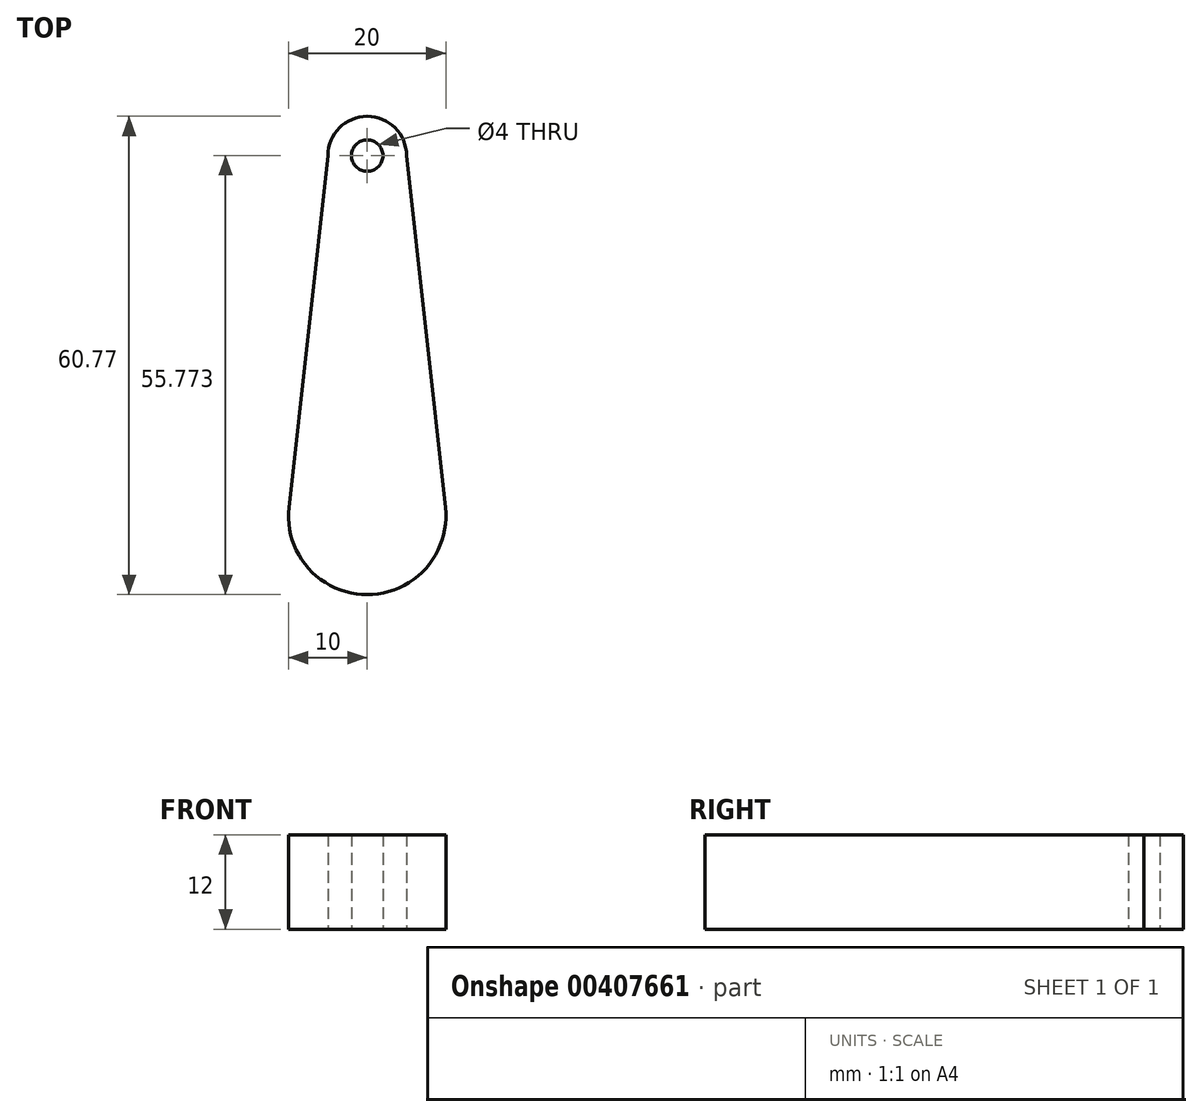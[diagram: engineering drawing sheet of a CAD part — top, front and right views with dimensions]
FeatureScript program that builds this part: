
annotation { "Feature Type Name" : "Feature", "Feature Type Description" : "" }
export const myFeature = defineFeature(function(context is Context, id is Id, definition is map)
    precondition{}
    {
        {
            var Q0;
            Q0=qCreatedBy(makeId("Top.planeOp"),FACE);
            var sketch = newSketch(context, id + "F0", { "sketchPlane" : qUnion([Q0])});
            skCircle(sketch, "E0", {"center": v(0, 0) * mm, "radius": 10 * mm});
            skCircle(sketch, "E1", {"center": v(0, 45.77) * mm, "radius": 5 * mm});
            skLineSegment(sketch, "E2", {"start": v(5, 45.77) * mm, "end": v(10.06, 0) * mm});
            skLineSegment(sketch, "E3", {"start": v(-5, 45.77) * mm, "end": v(-10.06, 0) * mm});
            skCircle(sketch, "E4", {"center": v(0, 45.77) * mm, "radius": 2 * mm});
            skSolve(sketch);
        }
        {
            var Q0;
            {var subQ0=sQuery(id+"F0.wireOp",EDGE,"E0");var subQ1=makeQuery(id+"F0.imprint","INTERSECT",VERTEX,{"derivedFrom":[subQ0,sQuery(id+"F0.wireOp",EDGE,"E2")]});Q0=makeQuery(id+"F0.imprint","IMPRINT",FACE,{"disambiguationData":[TD([[makeQuery(id+"F0.imprint","IMPRINT",EDGE,{"disambiguationData":[TD([[subQ1,-1.0]])],"derivedFrom":subQ0}),1.0]])]});}
            var Q1;
            {var subQ0=sQuery(id+"F0.wireOp",EDGE,"E1");var subQ1=makeQuery(id+"F0.imprint","INTERSECT",VERTEX,{"derivedFrom":[subQ0,sQuery(id+"F0.wireOp",EDGE,"E2")]});Q1=makeQuery(id+"F0.imprint","IMPRINT",FACE,{"disambiguationData":[TD([[makeQuery(id+"F0.imprint","IMPRINT",EDGE,{"disambiguationData":[TD([[subQ1,-1.0]])],"derivedFrom":subQ0}),1.0]])]});}
            var Q2;
            {var subQ0=sQuery(id+"F0.wireOp",EDGE,"E2");var subQ1=sQuery(id+"F0.wireOp",EDGE,"E0");var subQ2=makeQuery(id+"F0.imprint","INTERSECT",VERTEX,{"derivedFrom":[subQ1,subQ0]});Q2=makeQuery(id+"F0.imprint","IMPRINT",FACE,{"disambiguationData":[TD([[makeQuery(id+"F0.imprint","IMPRINT",EDGE,{"disambiguationData":[TD([[subQ2,-1.0]])],"derivedFrom":subQ1}),-1.0]])]});}
            extrude(context, id + "F1", {"entities" : qUnion([Q0, Q1, Q2]), "depth" : 12 * mm});
        }
    });
